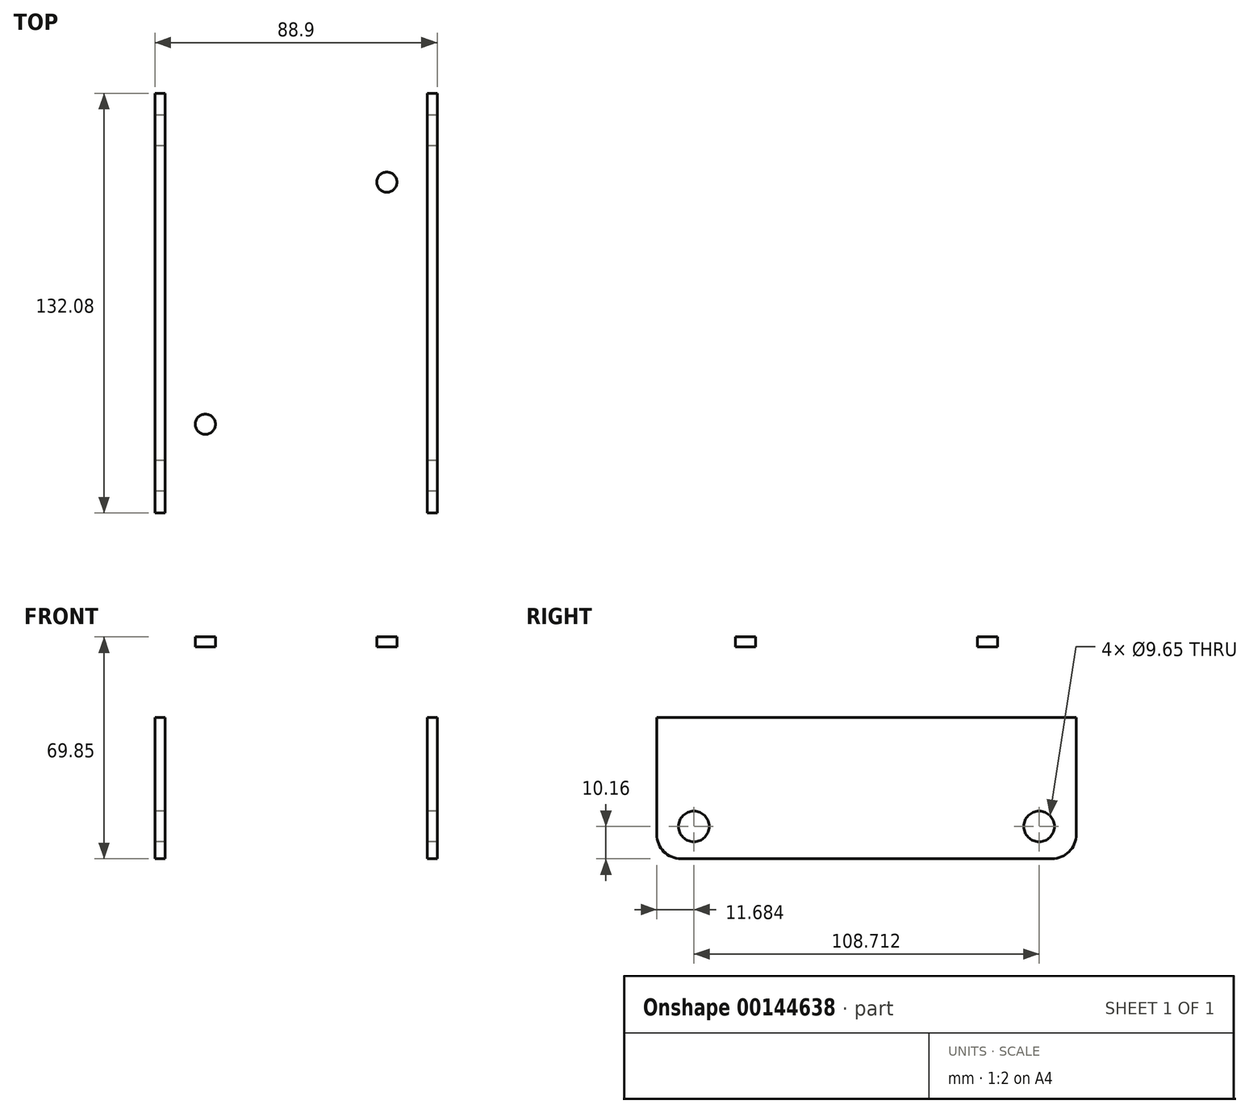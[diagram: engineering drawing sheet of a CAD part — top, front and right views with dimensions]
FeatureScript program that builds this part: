
annotation { "Feature Type Name" : "Feature", "Feature Type Description" : "" }
export const myFeature = defineFeature(function(context is Context, id is Id, definition is map)
    precondition{}
    {
        {
            var Q0;
            Q0=qCreatedBy(makeId("Right.planeOp"),FACE);
            var sketch = newSketch(context, id + "F0", { "sketchPlane" : qUnion([Q0])});
            skCircle(sketch, "E0", {"center": v(-54.36, 0) * mm, "radius": 4.83 * mm});
            skLineSegment(sketch, "E1.bottom", {"start": v(58.42, -10.16) * mm, "end": v(-58.42, -10.16) * mm});
            skLineSegment(sketch, "E1.top", {"start": v(66.04, 59.69) * mm, "end": v(-66.04, 59.7) * mm});
            skLineSegment(sketch, "E1.left", {"start": v(66.04, -2.54) * mm, "end": v(66.04, 59.7) * mm});
            skLineSegment(sketch, "E1.right", {"start": v(-66.04, -2.54) * mm, "end": v(-66.04, 59.69) * mm});
            skPoint(sketch, "E1.middle", {"position": v(0, 24.76) * mm});
            skPoint(sketch, "E2.visualSharp", {"position": v(-66.04, -10.16) * mm});
            skArc(sketch, "E2.filletArc", {"start": v(-66.04, -2.54) * mm, "mid": v(-63.8, -7.93) * mm, "end": v(-58.42, -10.16) * mm});
            skPoint(sketch, "E3.visualSharp", {"position": v(66.04, -10.16) * mm});
            skArc(sketch, "E3.filletArc", {"start": v(58.42, -10.16) * mm, "mid": v(63.8, -7.93) * mm, "end": v(66.04, -2.54) * mm});
            skCircle(sketch, "E4.MirrorC", {"center": v(54.36, 0) * mm, "radius": 4.83 * mm});
            skSolve(sketch);
        }
        {
            var Q0;
            Q0=makeQuery(id+"F0.imprint","IMPRINT",FACE,{"disambiguationData":[TD([[makeQuery(id+"F0.imprint","IMPRINT",EDGE,{"derivedFrom":sQuery(id+"F0.wireOp",EDGE,"E0")}),-1.0]])]});
            extrude(context, id + "F1", {"entities" : qUnion([Q0]), "depth" : 44.45 * mm, "hasSecondDirection" : true, "secondDirectionOppositeDirection" : true, "secondDirectionDepth" : 44.45 * mm});
        }
        {
            var Q0;
            Q0=qCreatedBy(makeId("Front.planeOp"),FACE);
            var sketch = newSketch(context, id + "F2", { "sketchPlane" : qUnion([Q0])});
            skLineSegment(sketch, "E5.0", {"start": v(41.28, -2.54) * mm, "end": v(41.28, -10.16) * mm});
            skLineSegment(sketch, "E5.1", {"start": v(-41.28, -2.54) * mm, "end": v(-41.28, -10.16) * mm});
            skLineSegment(sketch, "E5.2", {"start": v(-41.28, -2.54) * mm, "end": v(-41.28, 52.7) * mm});
            skLineSegment(sketch, "E5.3", {"start": v(37.47, 56.51) * mm, "end": v(-37.47, 56.51) * mm});
            skLineSegment(sketch, "E5.4", {"start": v(41.28, -2.54) * mm, "end": v(41.28, 52.7) * mm});
            skPoint(sketch, "E6.visualSharp", {"position": v(-41.28, 56.51) * mm});
            skArc(sketch, "E6.filletArc", {"start": v(-37.47, 56.51) * mm, "mid": v(-40.16, 55.4) * mm, "end": v(-41.28, 52.7) * mm});
            skPoint(sketch, "E7.visualSharp", {"position": v(41.28, 56.51) * mm});
            skArc(sketch, "E7.filletArc", {"start": v(41.28, 52.7) * mm, "mid": v(40.16, 55.4) * mm, "end": v(37.47, 56.51) * mm});
            skLineSegment(sketch, "E8", {"start": v(-41.28, -10.16) * mm, "end": v(41.28, -10.16) * mm});
            skSolve(sketch);
        }
        {
            var Q0;
            Q0=makeQuery(id+"F2.imprint","IMPRINT",FACE,{"disambiguationData":[TD([[makeQuery(id+"F2.imprint","IMPRINT",EDGE,{"derivedFrom":sQuery(id+"F2.wireOp",EDGE,"E5.0")}),-1.0]])]});
            extrude(context, id + "F3", {"entities" : qUnion([Q0]), "operationType" : NewBodyOperationType.REMOVE, "depth" : 76.2 * mm, "hasSecondDirection" : true, "secondDirectionOppositeDirection" : true, "secondDirectionDepth" : 76.2 * mm});
        }
        {
            var Q0;
            Q0=makeQuery(id+"F1.opExtrude","SWEPT_FACE",FACE,{"disambiguationData":[OSD([sQuery(id+"F0.wireOp",EDGE,"E1.top")])]});
            var sketch = newSketch(context, id + "F4", { "sketchPlane" : qUnion([Q0])});
            skCircle(sketch, "E9", {"center": v(28.57, -38.1) * mm, "radius": 3.18 * mm});
            skCircle(sketch, "E10.MirrorC", {"center": v(-28.57, -38.1) * mm, "radius": 3.18 * mm});
            skCircle(sketch, "E11.MirrorC", {"center": v(-28.57, 38.1) * mm, "radius": 3.18 * mm});
            skCircle(sketch, "E12.MirrorC", {"center": v(28.57, 38.1) * mm, "radius": 3.18 * mm});
            skSolve(sketch);
        }
        {
            var Q0;
            Q0=makeQuery(id+"F4.imprint","IMPRINT",FACE,{"disambiguationData":[TD([[makeQuery(id+"F4.imprint","IMPRINT",EDGE,{"derivedFrom":sQuery(id+"F4.wireOp",EDGE,"E9")}),1.0]])]});
            var Q1;
            Q1=makeQuery(id+"F4.imprint","IMPRINT",FACE,{"disambiguationData":[TD([[makeQuery(id+"F4.imprint","IMPRINT",EDGE,{"derivedFrom":sQuery(id+"F4.wireOp",EDGE,"E10.MirrorC")}),-1.0]])]});
            var Q2;
            Q2=makeQuery(id+"F4.imprint","IMPRINT",FACE,{"disambiguationData":[TD([[makeQuery(id+"F4.imprint","IMPRINT",EDGE,{"derivedFrom":sQuery(id+"F4.wireOp",EDGE,"E11.MirrorC")}),1.0]])]});
            var Q3;
            Q3=makeQuery(id+"F4.imprint","IMPRINT",FACE,{"disambiguationData":[TD([[makeQuery(id+"F4.imprint","IMPRINT",EDGE,{"derivedFrom":sQuery(id+"F4.wireOp",EDGE,"E12.MirrorC")}),-1.0]])]});
            extrude(context, id + "F5", {"entities" : qUnion([Q0, Q1, Q2, Q3]), "operationType" : NewBodyOperationType.REMOVE, "oppositeDirection" : true, "depth" : 25.4 * mm});
        }
    });
